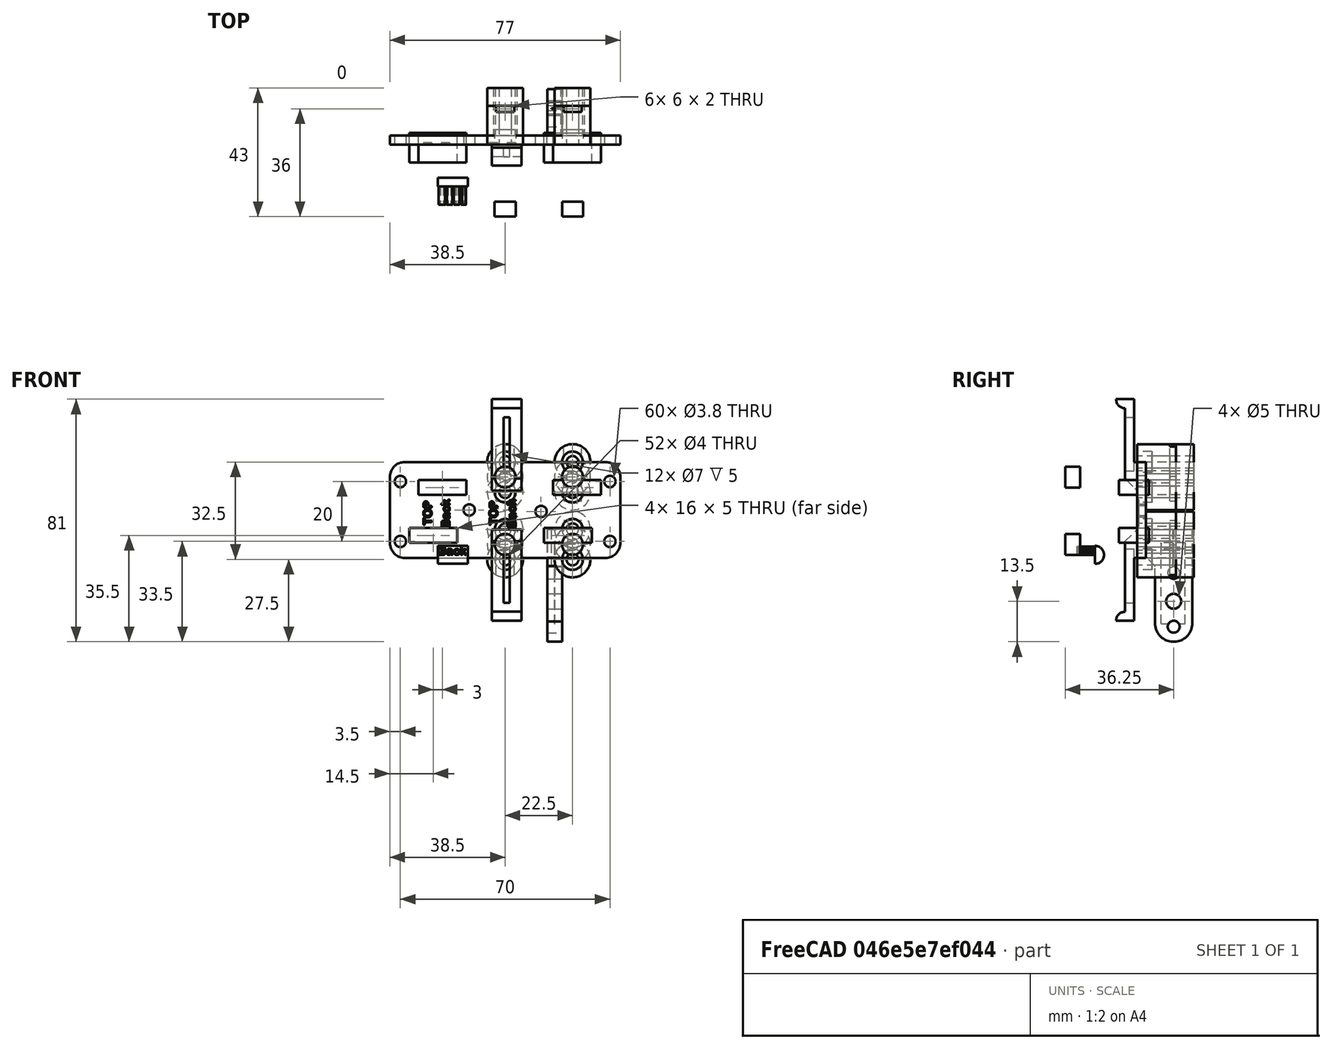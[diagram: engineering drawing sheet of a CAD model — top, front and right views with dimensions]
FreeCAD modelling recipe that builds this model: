
FCSTD DOCUMENT  (FreeCAD 0.16R6712 (Git))
Label: ParkingNozzleE3DV6Plate
License: All rights reserved
LicenseURL: http://en.wikipedia.org/wiki/All_rights_reserved
objects: Part::Cylinder×57, Part::MultiFuse×33, Part::Box×26, Part::Cut×23, Part::Feature×14, App::DocumentObjectGroup×7, Part::Part2DObjectPython×2, Part::Extrusion×1
note: 156 computed .brp shape members not serialized (recipe doc carries the construction recipe); baked Part::Feature solids carry a one-line shape summary decoded from their .brp

FEATURE [Part::Part2DObjectPython] ShapeString002  # Draft 2D object (typed FeaturePython)
  FontFile = <path>
  Size = 3
  String = TOP
  Tracking = 4
FEATURE [Part::Feature] Extrude001002001  label="Extrude001003"
  Placement = pos=(18,0,11) rot=(0,-1,0;1.5708rad)
  shape: bbox 2.835 x 6 x 7.877 mm, 76 faces, 3 solids (baked)
FEATURE [Part::Part2DObjectPython] ShapeString003  # Draft 2D object (typed FeaturePython)
  FontFile = <path>
  Size = 3
  String = Back
  Tracking = 4
FEATURE [Part::Extrusion] Extrude001002002
  Base = -> ShapeString003
  Dir = (0,0,6)
  Placement = pos=(0,0,0) rot=(1,0,0;1.5708rad)
  Solid = false
FEATURE [Part::Feature] Extrude001002002001  label="Extrude001002003"
  Placement = pos=(24,0,10) rot=(0,-1,0;1.5708rad)
  shape: bbox 2.835 x 6 x 9.142 mm, 140 faces, 4 solids (baked)
FEATURE [Part::Box] Box035  label="Würfel034"
  Height = 32
  Length = 77
  Placement = pos=(-16,14,-1) rot=(0,0,1;0rad)
  Width = 3
FEATURE [Part::MultiFuse] Fusion  label="Label"
  Placement = pos=(-20,14.6,-1) rot=(0,0,1;0rad)
  Shapes = -> [Extrude001002002001,Extrude001002001]
FEATURE [Part::Cut] Cut
  Base = -> Box035
  Tool = -> Fusion
FEATURE [Part::Box] Box  label="Würfel"
  Height = 21
  Length = 10
  Placement = pos=(0,0,-2) rot=(0,0,1;0rad)
  Width = 3
FEATURE [Part::Cylinder] Cylinder  label="Zylinder"
  Angle = 180
  Height = 10
  Placement = pos=(0,0,0) rot=(0,1,0;1.5708rad)
  Radius = 3
FEATURE [Part::Feature] Cylinder040  label="Zylinder031"
  Placement = pos=(0,0,-2) rot=(1,0,0;1.5708rad)
  shape: bbox 10 x 6 x 3 mm, 4 faces (baked)
FEATURE [Part::MultiFuse] Fusion026006
  Placement = pos=(18,10,-20) rot=(0,0,1;0rad)
  Shapes = -> [Box,Cylinder040]
FEATURE [Part::Box] Box036  label="Würfel035"
  Height = 21
  Length = 10
  Placement = pos=(0,0,-2) rot=(0,0,1;0rad)
  Width = 3
FEATURE [Part::Feature] Cylinder041  label="Zylinder032"
  Placement = pos=(0,0,-2) rot=(1,0,0;1.5708rad)
  shape: bbox 10 x 6 x 3 mm, 4 faces (baked)
FEATURE [Part::MultiFuse] Fusion026007
  Placement = pos=(28,10,50) rot=(0,1,0;3.14159rad)
  Shapes = -> [Box036,Cylinder041]
FEATURE [Part::Cylinder] Cylinder051  label="Zylinder042"
  Angle = 90
  Height = 40
  Placement = pos=(33,25,29) rot=(1,0,0;1.5708rad)
  Radius = 8
FEATURE [Part::Cylinder] Cylinder052  label="Zylinder043"
  Angle = 90
  Height = 40
  Placement = pos=(33,25,29) rot=(1,0,0;1.5708rad)
  Radius = 5
FEATURE [Part::Cut] Cut011004004
  Base = -> Cylinder051
  Placement = pos=(18,0,-7) rot=(0,-1,0;1.5708rad)
  Tool = -> Cylinder052
FEATURE [Part::Cylinder] Cylinder053  label="Zylinder044"
  Angle = 90
  Height = 40
  Placement = pos=(33,25,29) rot=(1,0,0;1.5708rad)
  Radius = 8
FEATURE [Part::Cylinder] Cylinder054  label="Zylinder045"
  Angle = 90
  Height = 40
  Placement = pos=(33,25,29) rot=(1,0,0;1.5708rad)
  Radius = 5
FEATURE [Part::Cut] Cut011004005
  Base = -> Cylinder053
  Placement = pos=(22,0,33) rot=(0,1,0;3.14159rad)
  Tool = -> Cylinder054
FEATURE [Part::Cylinder] Cylinder055  label="Zylinder046"
  Angle = 90
  Height = 40
  Placement = pos=(33,25,29) rot=(1,0,0;1.5708rad)
  Radius = 8
FEATURE [Part::Cylinder] Cylinder056  label="Zylinder047"
  Angle = 90
  Height = 40
  Placement = pos=(33,25,29) rot=(1,0,0;1.5708rad)
  Radius = 5
FEATURE [Part::Cut] Cut011004006
  Base = -> Cylinder055
  Placement = pos=(23,0,-3) rot=(0,0,1;0rad)
  Tool = -> Cylinder056
FEATURE [Part::Cylinder] Cylinder059  label="Zylinder050"
  Angle = 90
  Height = 40
  Placement = pos=(33,25,29) rot=(1,0,0;1.5708rad)
  Radius = 8
FEATURE [Part::Cylinder] Cylinder060  label="Zylinder051"
  Angle = 90
  Height = 40
  Placement = pos=(33,25,29) rot=(1,0,0;1.5708rad)
  Radius = 5
FEATURE [Part::Cut] Cut011004008
  Base = -> Cylinder059
  Placement = pos=(27,0,37) rot=(0,1,0;1.5708rad)
  Tool = -> Cylinder060
FEATURE [Part::MultiFuse] Fusion026012  label="RoundEdges"
  Shapes = -> [Cut011004008,Cut011004006,Cut011004004,Cut011004005]
FEATURE [Part::Box] Box037  label="Würfel036"
  Height = 10
  Length = 10
  Width = 4
FEATURE [Part::Box] Box038  label="Würfel037"
  Height = 10
  Length = 10
  Placement = pos=(0,-5,9) rot=(-1,0,0;0.785398rad)
  Width = 6
FEATURE [Part::Cut] Cut011004009
  Base = -> Box037
  Placement = pos=(18,10,-1) rot=(0,0,1;0rad)
  Tool = -> Box038
FEATURE [Part::Box] Box039  label="Würfel038"
  Height = 10
  Length = 10
  Width = 4
FEATURE [Part::Box] Box040  label="Würfel039"
  Height = 10
  Length = 10
  Placement = pos=(0,-5,9) rot=(-1,0,0;0.785398rad)
  Width = 6
FEATURE [Part::Cut] Cut011004010
  Base = -> Box039
  Placement = pos=(28,10,31) rot=(0,1,0;3.14159rad)
  Tool = -> Box040
FEATURE [Part::Box] Box041  label="Würfel040"
  Height = 18
  Length = 2
  Placement = pos=(22,-1,-16) rot=(0,0,1;0rad)
  Width = 14
FEATURE [Part::Box] Box042  label="Würfel041"
  Height = 18
  Length = 2
  Placement = pos=(22,-1,28) rot=(0,0,1;0rad)
  Width = 14
FEATURE [Part::MultiFuse] Fusion026013
  Shapes = -> [Fusion026007,Cut011004010]
FEATURE [Part::Cut] Cut011004011  label="DecuplerLeft"
  Base = -> Fusion026013
  Tool = -> Box042
FEATURE [Part::MultiFuse] Fusion026014
  Shapes = -> [Fusion026006,Cut011004009]
FEATURE [Part::Cut] Cut011004012  label="DecuplerRight"
  Base = -> Fusion026014
  Tool = -> Box041
FEATURE [Part::Cylinder] Cylinder034  label="Zylinder025"
  Angle = 360
  Height = 26
  Placement = pos=(-13,16,4.5) rot=(1,0,0;1.5708rad)
  Radius = 1.9
FEATURE [Part::Cylinder] Cylinder035  label="Zylinder026"
  Angle = 360
  Height = 26
  Placement = pos=(-13,16,24.5) rot=(1,0,0;1.5708rad)
  Radius = 1.9
FEATURE [Part::Cylinder] Cylinder036  label="Zylinder027"
  Angle = 360
  Height = 26
  Placement = pos=(10.5,16,15) rot=(1,0,0;1.5708rad)
  Radius = 1.9
FEATURE [Part::MultiFuse] Fusion026003
  Placement = pos=(0.5,0,0) rot=(0,0,1;0rad)
  Shapes = -> [Cylinder034,Cylinder035]
FEATURE [Part::Cylinder] Cylinder037  label="Zylinder028"
  Angle = 360
  Height = 26
  Placement = pos=(-13,16,4.5) rot=(1,0,0;1.5708rad)
  Radius = 1.9
FEATURE [Part::Cylinder] Cylinder038  label="Zylinder029"
  Angle = 360
  Height = 26
  Placement = pos=(-13,16,24.5) rot=(1,0,0;1.5708rad)
  Radius = 1.9
FEATURE [Part::MultiFuse] Fusion026004
  Placement = pos=(70.5,0,0) rot=(0,0,1;0rad)
  Shapes = -> [Cylinder037,Cylinder038]
FEATURE [Part::Cylinder] Cylinder039  label="Zylinder030"
  Angle = 360
  Height = 26
  Placement = pos=(34.5,16,14.5) rot=(1,0,0;1.5708rad)
  Radius = 1.9
FEATURE [Part::MultiFuse] Fusion026005  label="Bohrung"
  Placement = pos=(0,3,0) rot=(0,0,1;0rad)
  Shapes = -> [Cylinder036,Fusion026003,Fusion026004,Cylinder039]
FEATURE [Part::MultiFuse] Fusion026015
  Shapes = -> [Fusion026012,Fusion026005]
FEATURE [Part::Cut] Cut011004013  label="BasePlate"
  Base = -> Cut
  Tool = -> Fusion026015
FEATURE [Part::Box] Box034  label="Würfel033"
  Height = 5
  Length = 16
  Placement = pos=(-9.5,-18,4) rot=(0,0,1;0rad)
  Width = 10
FEATURE [Part::Box] Box043  label="Würfel042"
  Height = 5
  Length = 16
  Placement = pos=(35.5,-18,4) rot=(0,0,1;0rad)
  Width = 10
FEATURE [Part::Box] Box044  label="Würfel043"
  Height = 5
  Length = 16
  Placement = pos=(-6.5,-18,20) rot=(0,0,1;0rad)
  Width = 10
FEATURE [Part::Box] Box045  label="Würfel044"
  Height = 5
  Length = 16
  Placement = pos=(38.5,-18,20) rot=(0,0,1;0rad)
  Width = 10
FEATURE [Part::MultiFuse] Fusion026017  label="SripperHoles"
  Placement = pos=(0,26,0) rot=(0,0,1;0rad)
  Shapes = -> [Box034,Box045,Box043,Box044]
FEATURE [Part::Feature] Cut011004014001  label="BasePlateOpen_export"
  shape: bbox 77 x 3 x 32 mm, 246 faces (baked)
FEATURE [Part::Feature] Cut011004013001  label="BasePlate_export"
  shape: bbox 77 x 3 x 32 mm, 230 faces (baked)
FEATURE [Part::Cylinder] Cylinder061  label="Zylinder052"
  Angle = 360
  Height = 20
  Placement = pos=(-3.5,14,0) rot=(0,0,1;0rad)
  Radius = 2
FEATURE [Part::Cylinder] Cylinder001  label="Zylinder001"
  Angle = 360
  Height = 20
  Placement = pos=(-3.5,36.5,0) rot=(0,0,1;0rad)
  Radius = 2
FEATURE [Part::Cylinder] Cylinder002  label="Zylinder002"
  Angle = 360
  Height = 20
  Placement = pos=(19,14,0) rot=(0,0,1;0rad)
  Radius = 2
FEATURE [Part::Cylinder] Cylinder003  label="Zylinder003"
  Angle = 360
  Height = 20
  Placement = pos=(19,36.5,0) rot=(0,0,1;0rad)
  Radius = 2
FEATURE [Part::MultiFuse] Fusion026018
  Placement = pos=(26,10,-10.5) rot=(1,0,0;1.5708rad)
  Shapes = -> [Cylinder061,Cylinder002,Cylinder003,Cylinder001]
FEATURE [Part::Cylinder] Cylinder062  label="Zylinder053"
  Angle = 360
  Height = 5
  Placement = pos=(-3.5,14,0) rot=(0,0,1;0rad)
  Radius = 3.5
FEATURE [Part::Cylinder] Cylinder063  label="Zylinder054"
  Angle = 360
  Height = 5
  Placement = pos=(-3.5,36.5,0) rot=(0,0,1;0rad)
  Radius = 3.5
FEATURE [Part::Cylinder] Cylinder064  label="Zylinder055"
  Angle = 360
  Height = 5
  Placement = pos=(19,14,0) rot=(0,0,1;0rad)
  Radius = 3.5
FEATURE [Part::Cylinder] Cylinder065  label="Zylinder056"
  Angle = 360
  Height = 5
  Placement = pos=(19,36.5,0) rot=(0,0,1;0rad)
  Radius = 3.5
FEATURE [Part::MultiFuse] Fusion026019
  Placement = pos=(26,-5,-10.5) rot=(1,0,0;1.5708rad)
  Shapes = -> [Cylinder062,Cylinder064,Cylinder065,Cylinder063]
FEATURE [Part::Cylinder] Cylinder066  label="Zylinder057"
  Angle = 360
  Height = 13
  Placement = pos=(-3.5,14,0) rot=(0,0,1;0rad)
  Radius = 6
FEATURE [Part::Cylinder] Cylinder067  label="Zylinder058"
  Angle = 360
  Height = 13
  Placement = pos=(-3.5,36.5,0) rot=(0,0,1;0rad)
  Radius = 6
FEATURE [Part::Cylinder] Cylinder068  label="Zylinder059"
  Angle = 360
  Height = 13
  Placement = pos=(19,14,0) rot=(0,0,1;0rad)
  Radius = 6
FEATURE [Part::Cylinder] Cylinder069  label="Zylinder060"
  Angle = 360
  Height = 13
  Placement = pos=(19,36.5,0) rot=(0,0,1;0rad)
  Radius = 6
FEATURE [Part::MultiFuse] Fusion026020  label="E3DV6Mount_Base"
  Placement = pos=(26,27,-15.5) rot=(1,0,0;1.5708rad)
  Shapes = -> [Cylinder066,Cylinder068,Cylinder069,Cylinder067]
FEATURE [Part::MultiFuse] Fusion026021  label="E3DV6Mount_Bohrung"
  Placement = pos=(0,24,-5) rot=(0,0,1;0rad)
  Shapes = -> [Fusion026018,Fusion026019]
FEATURE [Part::MultiFuse] Fusion026022  label="E3DV6Mount_Full"
  Shapes = -> [Fusion026020,Cut011004013]
FEATURE [Part::Cut] Cut011004014002  label="E3DV6Mount"
  Base = -> Fusion026022
  Tool = -> Fusion026021
FEATURE [Part::Feature] Cut011004014002001  label="E3DV6Mount001"
  shape: bbox 77 x 13 x 38 mm, 252 faces (baked)
FEATURE [Part::Feature] Cut011004014002002  label="E3DV6Mount002"
  shape: bbox 77 x 13 x 38.5 mm, 252 faces (baked)
FEATURE [Part::Feature] Extrude001002002002  label="Extrude001002002004"
  Placement = pos=(18,0,11) rot=(0,-1,0;1.5708rad)
  shape: bbox 2.835 x 6 x 7.877 mm, 76 faces, 3 solids (baked)
FEATURE [Part::Feature] Extrude001002002003  label="Extrude001002002005"
  Placement = pos=(24,0,10) rot=(0,-1,0;1.5708rad)
  shape: bbox 2.835 x 6 x 9.142 mm, 140 faces, 4 solids (baked)
FEATURE [Part::Box] Box046  label="Würfel045"
  Height = 32
  Length = 77
  Placement = pos=(-16,14,-1) rot=(0,0,1;0rad)
  Width = 3
FEATURE [Part::MultiFuse] Fusion026023  label="Label001"
  Placement = pos=(-20,14.6,-1) rot=(0,0,1;0rad)
  Shapes = -> [Extrude001002002003,Extrude001002002002]
FEATURE [Part::Cut] Cut011004014002003
  Base = -> Box046
  Tool = -> Fusion026023
FEATURE [Part::Cylinder] Cylinder070  label="Zylinder061"
  Angle = 90
  Height = 40
  Placement = pos=(33,25,29) rot=(1,0,0;1.5708rad)
  Radius = 8
FEATURE [Part::Cylinder] Cylinder071  label="Zylinder062"
  Angle = 90
  Height = 40
  Placement = pos=(33,25,29) rot=(1,0,0;1.5708rad)
  Radius = 5
FEATURE [Part::Cut] Cut011004014002004
  Base = -> Cylinder070
  Placement = pos=(18,0,-7) rot=(0,-1,0;1.5708rad)
  Tool = -> Cylinder071
FEATURE [Part::Cylinder] Cylinder072  label="Zylinder063"
  Angle = 90
  Height = 40
  Placement = pos=(33,25,29) rot=(1,0,0;1.5708rad)
  Radius = 8
FEATURE [Part::Cylinder] Cylinder073  label="Zylinder064"
  Angle = 90
  Height = 40
  Placement = pos=(33,25,29) rot=(1,0,0;1.5708rad)
  Radius = 5
FEATURE [Part::Cut] Cut011004014002005
  Base = -> Cylinder072
  Placement = pos=(22,0,33) rot=(0,1,0;3.14159rad)
  Tool = -> Cylinder073
FEATURE [Part::Cylinder] Cylinder074  label="Zylinder065"
  Angle = 90
  Height = 40
  Placement = pos=(33,25,29) rot=(1,0,0;1.5708rad)
  Radius = 8
FEATURE [Part::Cylinder] Cylinder075  label="Zylinder066"
  Angle = 90
  Height = 40
  Placement = pos=(33,25,29) rot=(1,0,0;1.5708rad)
  Radius = 5
FEATURE [Part::Cut] Cut011004014002006
  Base = -> Cylinder074
  Placement = pos=(23,0,-3) rot=(0,0,1;0rad)
  Tool = -> Cylinder075
FEATURE [Part::Cylinder] Cylinder076  label="Zylinder067"
  Angle = 90
  Height = 40
  Placement = pos=(33,25,29) rot=(1,0,0;1.5708rad)
  Radius = 8
FEATURE [Part::Cylinder] Cylinder077  label="Zylinder068"
  Angle = 90
  Height = 40
  Placement = pos=(33,25,29) rot=(1,0,0;1.5708rad)
  Radius = 5
FEATURE [Part::Cut] Cut011004014002007
  Base = -> Cylinder076
  Placement = pos=(27,0,37) rot=(0,1,0;1.5708rad)
  Tool = -> Cylinder077
FEATURE [Part::MultiFuse] Fusion026024  label="RoundEdges001"
  Shapes = -> [Cut011004014002007,Cut011004014002006,Cut011004014002004,Cut011004014002005]
FEATURE [Part::Cylinder] Cylinder078  label="Zylinder069"
  Angle = 360
  Height = 26
  Placement = pos=(-13,16,4.5) rot=(1,0,0;1.5708rad)
  Radius = 1.9
FEATURE [Part::Cylinder] Cylinder079  label="Zylinder070"
  Angle = 360
  Height = 26
  Placement = pos=(-13,16,24.5) rot=(1,0,0;1.5708rad)
  Radius = 1.9
FEATURE [Part::Cylinder] Cylinder080  label="Zylinder071"
  Angle = 360
  Height = 26
  Placement = pos=(10.5,16,15) rot=(1,0,0;1.5708rad)
  Radius = 1.9
FEATURE [Part::MultiFuse] Fusion026025
  Placement = pos=(0.5,0,0) rot=(0,0,1;0rad)
  Shapes = -> [Cylinder078,Cylinder079]
FEATURE [Part::Cylinder] Cylinder081  label="Zylinder072"
  Angle = 360
  Height = 26
  Placement = pos=(-13,16,4.5) rot=(1,0,0;1.5708rad)
  Radius = 1.9
FEATURE [Part::Cylinder] Cylinder082  label="Zylinder073"
  Angle = 360
  Height = 26
  Placement = pos=(-13,16,24.5) rot=(1,0,0;1.5708rad)
  Radius = 1.9
FEATURE [Part::MultiFuse] Fusion026026
  Placement = pos=(70.5,0,0) rot=(0,0,1;0rad)
  Shapes = -> [Cylinder081,Cylinder082]
FEATURE [Part::Cylinder] Cylinder083  label="Zylinder074"
  Angle = 360
  Height = 26
  Placement = pos=(34.5,16,14.5) rot=(1,0,0;1.5708rad)
  Radius = 1.9
FEATURE [Part::MultiFuse] Fusion026027  label="Bohrung001"
  Placement = pos=(0,3,0) rot=(0,0,1;0rad)
  Shapes = -> [Cylinder080,Fusion026025,Fusion026026,Cylinder083]
FEATURE [Part::MultiFuse] Fusion026028
  Shapes = -> [Fusion026024,Fusion026027]
FEATURE [Part::Cut] Cut011004014002008  label="BasePlate001"
  Base = -> Cut011004014002003
  Tool = -> Fusion026028
FEATURE [Part::Cylinder] Cylinder084  label="Zylinder075"
  Angle = 360
  Height = 20
  Placement = pos=(-3.5,14,0) rot=(0,0,1;0rad)
  Radius = 2
FEATURE [Part::Cylinder] Cylinder085  label="Zylinder076"
  Angle = 360
  Height = 20
  Placement = pos=(-3.5,36.5,0) rot=(0,0,1;0rad)
  Radius = 2
FEATURE [Part::Cylinder] Cylinder086  label="Zylinder077"
  Angle = 360
  Height = 20
  Placement = pos=(19,14,0) rot=(0,0,1;0rad)
  Radius = 2
FEATURE [Part::Cylinder] Cylinder087  label="Zylinder078"
  Angle = 360
  Height = 20
  Placement = pos=(19,36.5,0) rot=(0,0,1;0rad)
  Radius = 2
FEATURE [Part::MultiFuse] Fusion026029  label="Bohrloch"
  Placement = pos=(26,10,-10.5) rot=(1,0,0;1.5708rad)
  Shapes = -> [Cylinder084,Cylinder086,Cylinder087,Cylinder085]
FEATURE [Part::Cylinder] Cylinder088  label="Zylinder079"
  Angle = 360
  Height = 5
  Placement = pos=(-3.5,14,0) rot=(0,0,1;0rad)
  Radius = 3.5
FEATURE [Part::Cylinder] Cylinder089  label="Zylinder080"
  Angle = 360
  Height = 5
  Placement = pos=(-3.5,36.5,0) rot=(0,0,1;0rad)
  Radius = 3.5
FEATURE [Part::Cylinder] Cylinder090  label="Zylinder081"
  Angle = 360
  Height = 5
  Placement = pos=(19,14,0) rot=(0,0,1;0rad)
  Radius = 3.5
FEATURE [Part::Cylinder] Cylinder091  label="Zylinder082"
  Angle = 360
  Height = 5
  Placement = pos=(19,36.5,0) rot=(0,0,1;0rad)
  Radius = 3.5
FEATURE [Part::MultiFuse] Fusion026030  label="MutterSenke"
  Placement = pos=(26,-5,-10.5) rot=(1,0,0;1.5708rad)
  Shapes = -> [Cylinder088,Cylinder090,Cylinder091,Cylinder089]
FEATURE [Part::Cylinder] Cylinder092  label="Zylinder083"
  Angle = 360
  Height = 19
  Placement = pos=(-3.5,14,0) rot=(0,0,1;0rad)
  Radius = 6
FEATURE [Part::Cylinder] Cylinder093  label="Zylinder084"
  Angle = 360
  Height = 19
  Placement = pos=(-3.5,36.5,0) rot=(0,0,1;0rad)
  Radius = 6
FEATURE [Part::Cylinder] Cylinder094  label="Zylinder085"
  Angle = 360
  Height = 19
  Placement = pos=(19,14,0) rot=(0,0,1;0rad)
  Radius = 6
FEATURE [Part::Cylinder] Cylinder095  label="Zylinder086"
  Angle = 360
  Height = 19
  Placement = pos=(19,36.5,0) rot=(0,0,1;0rad)
  Radius = 6
FEATURE [Part::MultiFuse] Fusion026031  label="E3DV6Mount_Base001"
  Placement = pos=(26,33,-10.5) rot=(1,0,0;1.5708rad)
  Shapes = -> [Cylinder092,Cylinder094,Cylinder095,Cylinder093]
FEATURE [Part::MultiFuse] Fusion026033  label="E3DV6Mount_Full001"
  Shapes = -> [Fusion026031,Cut011004014002008]
FEATURE [Part::Box] Box047  label="Würfel046"
  Height = 12
  Length = 6
  Placement = pos=(19.5,-4,23) rot=(0,0,1;0rad)
  Width = 2
FEATURE [Part::Box] Box048  label="Würfel047"
  Height = 12
  Length = 6
  Placement = pos=(42,-4,-5.5) rot=(0,0,1;0rad)
  Width = 2
FEATURE [Part::Box] Box049  label="Würfel048"
  Height = 12
  Length = 6
  Placement = pos=(19.5,-4,-5.5) rot=(0,0,1;0rad)
  Width = 2
FEATURE [Part::Box] Box050  label="Würfel049"
  Height = 12
  Length = 6
  Placement = pos=(42,-4,23) rot=(0,0,1;0rad)
  Width = 2
FEATURE [Part::MultiFuse] Fusion026034  label="MutterSchlitz"
  Placement = pos=(0,5,0) rot=(0,0,1;0rad)
  Shapes = -> [Box047,Box048,Box049,Box050]
FEATURE [Part::MultiFuse] Fusion026035  label="Bohrung002"
  Placement = pos=(0,24,0) rot=(0,0,1;0rad)
  Shapes = -> [Fusion026029,Fusion026034]
FEATURE [Part::Box] Box051  label="Würfel050"
  Height = 7
  Length = 57
  Placement = pos=(0,13,-8) rot=(0,0,1;0rad)
  Width = 20
FEATURE [Part::Box] Box052  label="Würfel051"
  Height = 7
  Length = 57
  Placement = pos=(0,13,31) rot=(0,0,1;0rad)
  Width = 20
FEATURE [Part::MultiFuse] Fusion026036  label="SideCut"
  Shapes = -> [Box051,Box052]
FEATURE [Part::Cut] Cut011004014002009002
  Base = -> Fusion026033
  Tool = -> Fusion026035
FEATURE [Part::Feature] Cut011004014002009002001  label="PrusaAdapterLeft"
  shape: bbox 77 x 19 x 38 mm, 268 faces (baked)
FEATURE [Part::Feature] Cut011004014002009002002  label="PrusaAdapterRight"
  shape: bbox 77 x 19 x 38.5 mm, 268 faces (baked)
FEATURE [Part::Cut] Cut011004014002009002003
  Base = -> Cut011004014002009002
  Tool = -> Fusion026036
FEATURE [Part::Feature] Cut011004014002009002003001  label="PrusaAdapterCenter"
  shape: bbox 77 x 19 x 32 mm, 266 faces (baked)
FEATURE [Part::Box] Box053  label="BLT_MountPlate"
  Height = 37.5
  Length = 5
  Placement = pos=(25,20,-29) rot=(0,0,1;0rad)
  Width = 12.5
FEATURE [Part::Cylinder] Cylinder096  label="Cylinder"
  Angle = 360
  Height = 10
  Placement = pos=(34,-27,-18) rot=(0,1,0;1.5708rad)
  Radius = 2
FEATURE [Part::Cylinder] Cylinder097  label="Cylinder001"
  Angle = 360
  Height = 10
  Placement = pos=(34,-27,-36) rot=(0,1,0;1.5708rad)
  Radius = 2
FEATURE [Part::Cylinder] Cylinder098  label="Cylinder002"
  Angle = 360
  Height = 10
  Placement = pos=(34,-27,-27.5) rot=(0,1,0;1.5708rad)
  Radius = 2.5
FEATURE [Part::MultiFuse] Fusion026037  label="BLT_Bohrung"
  Placement = pos=(-11,53.25,12) rot=(0,0,1;0rad)
  Shapes = -> [Cylinder096,Cylinder097,Cylinder098]
FEATURE [Part::Box] Box054  label="Cube"
  Height = 14.5
  Length = 5
  Placement = pos=(25,15,-6) rot=(0,0,1;0rad)
  Width = 5
FEATURE [Part::Box] Box055  label="Cube001"
  Height = 10
  Length = 10
  Placement = pos=(22,15,-12.8) rot=(1,0,0;0.785398rad)
  Width = 10
FEATURE [Part::Cut] Cut011004014002009002003002
  Base = -> Box054
  Tool = -> Box055
FEATURE [Part::Cut] Cut011004014002009002003003
  Base = -> Box053
  Tool = -> Fusion026037
FEATURE [Part::MultiFuse] Fusion026038
  Placement = pos=(11.6,0,0) rot=(0,0,1;0rad)
  Shapes = -> [Cut011004014002009002003002,Cut011004014002009002003003]
FEATURE [Part::Box] Box056  label="Cube002"
  Height = 12.5
  Length = 12.5
  Width = 12.5
FEATURE [Part::Cylinder] Cylinder099  label="Cylinder003"
  Angle = 360
  Height = 12.5
  Placement = pos=(0,6.25,12) rot=(0,1,0;1.5708rad)
  Radius = 6.25
FEATURE [Part::Cut] Cut011004014002009002003004
  Base = -> Box056
  Placement = pos=(32,20,-34.8) rot=(0,0,1;0rad)
  Tool = -> Cylinder099
FEATURE [Part::Box] Box057  label="Schlitz"
  Height = 15
  Length = 4
  Placement = pos=(38,26,-5) rot=(0,0,1;0rad)
  Width = 0.2
FEATURE [Part::Box] Box058  label="Schlitz001"
  Height = 27
  Length = 0.2
  Placement = pos=(39,22,-23) rot=(0,0,1;0rad)
  Width = 8
FEATURE [Part::MultiFuse] Fusion026039  label="CutOut"
  Shapes = -> [Cut011004014002009002003004,Box058,Box057]
FEATURE [Part::Cut] Cut011004014002009002003005
  Base = -> Fusion026038
  Tool = -> Fusion026039
FEATURE [Part::MultiFuse] Fusion026040  label="PrusaBLTAdapter"
  Shapes = -> [Cut011004014002009002003001,Cut011004014002009002003005]
FEATURE [Part::Feature] Fusion026040001  label="PrusaBLTAdapter001"
  shape: bbox 77 x 19 x 60 mm, 300 faces (baked)
FEATURE [App::DocumentObjectGroup] Group  label="Model_00"
  Group = -> [Fusion026040001,Cut011004014001,Cut011004013001,Cut011004014002009002001,Cut011004014002009002002,Cut011004014002001,Cut011004014002002]
FEATURE [App::DocumentObjectGroup] Group001  label="__COLLECTION__"
  Group = -> [Fusion026030,Fusion026017]
FEATURE [App::DocumentObjectGroup] Group002  label="__DRAFT__"
  Group = -> [ShapeString002,Extrude001002002,Cylinder]
FEATURE [App::DocumentObjectGroup] Group006  label="PrusaAdapter"
  Group = -> [Cut011004014002009002003,Cut011004014002]
FEATURE [App::DocumentObjectGroup] Group007  label="BasePlate_Front"
FEATURE [App::DocumentObjectGroup] Group008  label="BasePlate_Back"
  Group = -> [Cut011004011,Cut011004012]
FEATURE [App::DocumentObjectGroup] Group009  label="PrusaBLTAdapter002"
  Group = -> [Fusion026040]
note: 2 file-system paths scrubbed to <path> (originals preserved in the JSON sidecar)
